# Revit family: НЕВАТОМ_Клапан KPNZ-60(90)-D-NP-04(12)-МN, Версия 2
name_source: partatom
category: Арматура воздуховодов
revit_build: Autodesk Revit 2017 (Build: 20170118_1100(x64)
units: mm (PartAtom-declared; Revit-internal decimal feet)

## family parameters
Всегда вертикально = Нет
На основе рабочей плоскости = Нет
Общий = Нет
При загрузке вырезать с полостями = Нет
Размер круглого соединителя = Использовать диаметр
Тип детали = Вставляется

## types (2) — shared parameters
ADSK_Единица измерения = шт.
ADSK_Завод-изготовитель = НЕВАТОМ
ADSK_Количество = 1
ADSK_Материал наименование = Оцинкованная сталь
ADSK_Потеря давления воздуха = 0.0 Па
ADSK_Расход воздуха = 0.0 л/с
ADSK_Ток = 0 А
H = 140 мм
L = 320 мм
L np = 30 мм
L1 = 320 мм
Nevatom_URL = https://t.me
P = 200 мм
d = 9 мм
t = 1 мм
Высота привода = 100 мм
Длина площадки = 150 мм
Материал корпуса = Материал корпуса
Ширина площадки = 98 мм
Ширина привода = 100 мм
zero-valued in all types: a

## per-type parameters (varying)
| type | Закрыто | Открыто |
| KPNZ-60(90)-D-NP-04(12)-MN | Нет | Да |
| KPNZ-60(90)-D-NP-04-MN | Да | Нет |
